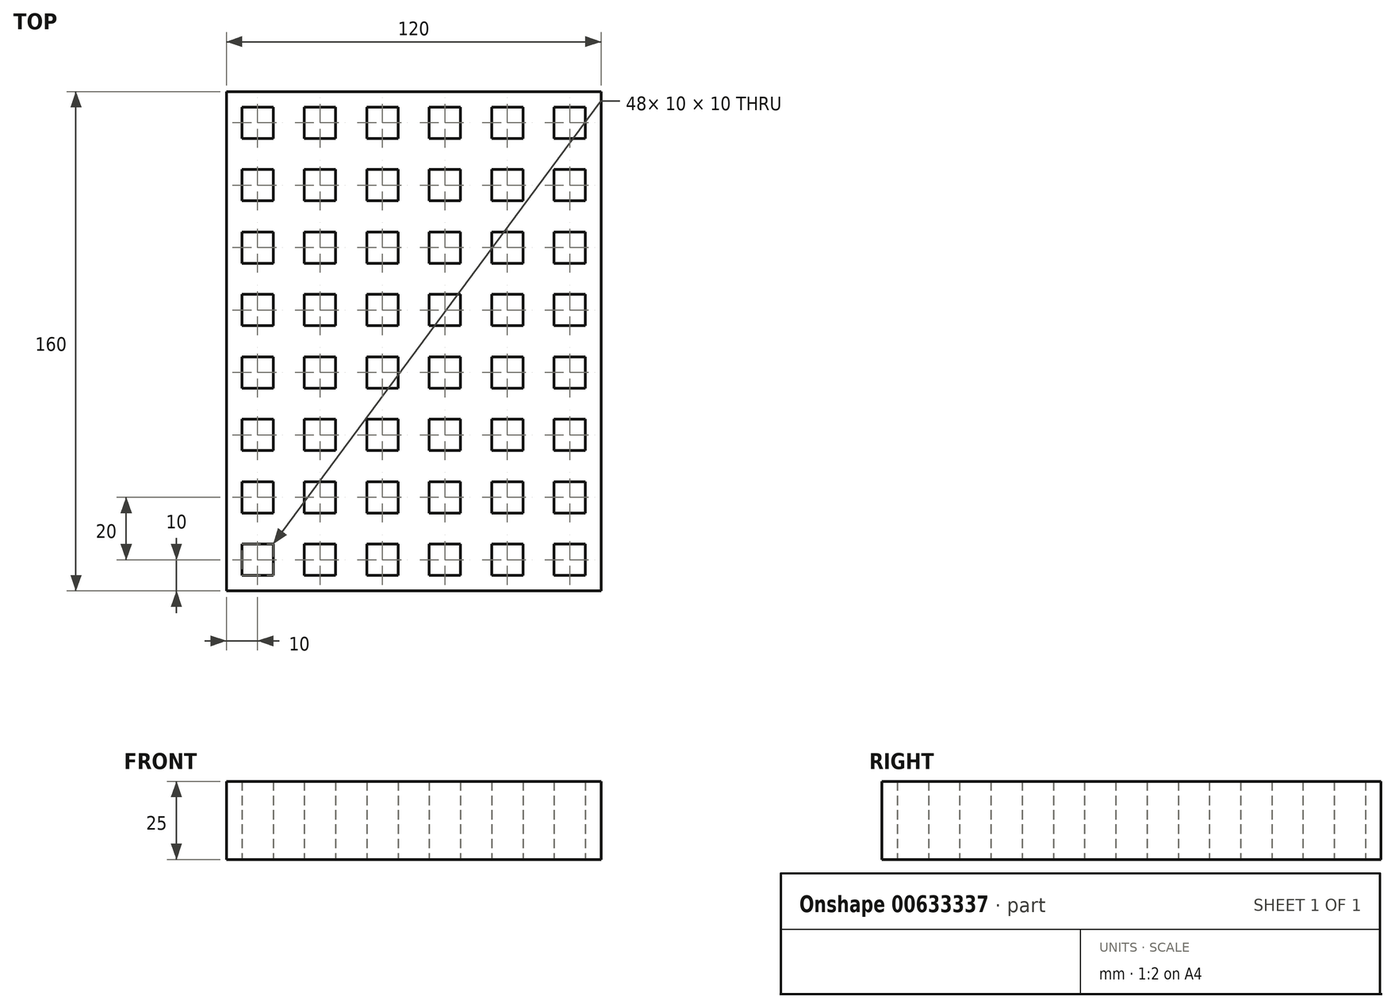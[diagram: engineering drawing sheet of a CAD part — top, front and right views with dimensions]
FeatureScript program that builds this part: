
annotation { "Feature Type Name" : "Feature", "Feature Type Description" : "" }
export const myFeature = defineFeature(function(context is Context, id is Id, definition is map)
    precondition{}
    {
        {
            var Q0;
            Q0=qCreatedBy(makeId("Top.planeOp"),FACE);
            var sketch = newSketch(context, id + "F0", { "sketchPlane" : qUnion([Q0])});
            skLineSegment(sketch, "E0.bottom", {"start": v(60, 80) * mm, "end": v(-60, 80) * mm});
            skLineSegment(sketch, "E0.top", {"start": v(60, -80) * mm, "end": v(-60, -80) * mm});
            skLineSegment(sketch, "E0.left", {"start": v(60, 80) * mm, "end": v(60, -80) * mm});
            skLineSegment(sketch, "E0.right", {"start": v(-60, 80) * mm, "end": v(-60, -80) * mm});
            skPoint(sketch, "E0.middle", {"position": v(0, 0) * mm});
            skLineSegment(sketch, "E1", {"start": v(-60, 80) * mm, "end": v(-60, 75) * mm, "construction": true});
            skLineSegment(sketch, "E2", {"start": v(-60, 75) * mm, "end": v(-55, 75) * mm, "construction": true});
            skLineSegment(sketch, "E3.bottom", {"start": v(-55, 75) * mm, "end": v(-45, 75) * mm});
            skLineSegment(sketch, "E3.top", {"start": v(-55, 65) * mm, "end": v(-45, 65) * mm});
            skLineSegment(sketch, "E3.left", {"start": v(-55, 75) * mm, "end": v(-55, 65) * mm});
            skLineSegment(sketch, "E3.right", {"start": v(-45, 75) * mm, "end": v(-45, 65) * mm});
            skLineSegment(sketch, "E4.0.1.0", {"start": v(-55, 55) * mm, "end": v(-45, 55) * mm});
            skLineSegment(sketch, "E4.0.1.1", {"start": v(-45, 55) * mm, "end": v(-45, 45) * mm});
            skLineSegment(sketch, "E4.0.1.2", {"start": v(-55, 45) * mm, "end": v(-45, 45) * mm});
            skLineSegment(sketch, "E4.0.1.3", {"start": v(-55, 55) * mm, "end": v(-55, 45) * mm});
            skLineSegment(sketch, "E4.0.2.0", {"start": v(-55, 35) * mm, "end": v(-45, 35) * mm});
            skLineSegment(sketch, "E4.0.2.1", {"start": v(-45, 35) * mm, "end": v(-45, 25) * mm});
            skLineSegment(sketch, "E4.0.2.2", {"start": v(-55, 25) * mm, "end": v(-45, 25) * mm});
            skLineSegment(sketch, "E4.0.2.3", {"start": v(-55, 35) * mm, "end": v(-55, 25) * mm});
            skLineSegment(sketch, "E4.0.3.0", {"start": v(-55, 15) * mm, "end": v(-45, 15) * mm});
            skLineSegment(sketch, "E4.0.3.1", {"start": v(-45, 15) * mm, "end": v(-45, 5) * mm});
            skLineSegment(sketch, "E4.0.3.2", {"start": v(-55, 5) * mm, "end": v(-45, 5) * mm});
            skLineSegment(sketch, "E4.0.3.3", {"start": v(-55, 15) * mm, "end": v(-55, 5) * mm});
            skLineSegment(sketch, "E4.0.4.0", {"start": v(-55, -5) * mm, "end": v(-45, -5) * mm});
            skLineSegment(sketch, "E4.0.4.1", {"start": v(-45, -5) * mm, "end": v(-45, -15) * mm});
            skLineSegment(sketch, "E4.0.4.2", {"start": v(-55, -15) * mm, "end": v(-45, -15) * mm});
            skLineSegment(sketch, "E4.0.4.3", {"start": v(-55, -5) * mm, "end": v(-55, -15) * mm});
            skLineSegment(sketch, "E4.0.5.0", {"start": v(-55, -25) * mm, "end": v(-45, -25) * mm});
            skLineSegment(sketch, "E4.0.5.1", {"start": v(-45, -25) * mm, "end": v(-45, -35) * mm});
            skLineSegment(sketch, "E4.0.5.2", {"start": v(-55, -35) * mm, "end": v(-45, -35) * mm});
            skLineSegment(sketch, "E4.0.5.3", {"start": v(-55, -25) * mm, "end": v(-55, -35) * mm});
            skLineSegment(sketch, "E4.0.6.0", {"start": v(-55, -45) * mm, "end": v(-45, -45) * mm});
            skLineSegment(sketch, "E4.0.6.1", {"start": v(-45, -45) * mm, "end": v(-45, -55) * mm});
            skLineSegment(sketch, "E4.0.6.2", {"start": v(-55, -55) * mm, "end": v(-45, -55) * mm});
            skLineSegment(sketch, "E4.0.6.3", {"start": v(-55, -45) * mm, "end": v(-55, -55) * mm});
            skLineSegment(sketch, "E4.0.7.0", {"start": v(-55, -65) * mm, "end": v(-45, -65) * mm});
            skLineSegment(sketch, "E4.0.7.1", {"start": v(-45, -65) * mm, "end": v(-45, -75) * mm});
            skLineSegment(sketch, "E4.0.7.2", {"start": v(-55, -75) * mm, "end": v(-45, -75) * mm});
            skLineSegment(sketch, "E4.0.7.3", {"start": v(-55, -65) * mm, "end": v(-55, -75) * mm});
            skLineSegment(sketch, "E4.1.0.0", {"start": v(-35, 75) * mm, "end": v(-25, 75) * mm});
            skLineSegment(sketch, "E4.1.0.1", {"start": v(-25, 75) * mm, "end": v(-25, 65) * mm});
            skLineSegment(sketch, "E4.1.0.2", {"start": v(-35, 65) * mm, "end": v(-25, 65) * mm});
            skLineSegment(sketch, "E4.1.0.3", {"start": v(-35, 75) * mm, "end": v(-35, 65) * mm});
            skLineSegment(sketch, "E4.1.1.0", {"start": v(-35, 55) * mm, "end": v(-25, 55) * mm});
            skLineSegment(sketch, "E4.1.1.1", {"start": v(-25, 55) * mm, "end": v(-25, 45) * mm});
            skLineSegment(sketch, "E4.1.1.2", {"start": v(-35, 45) * mm, "end": v(-25, 45) * mm});
            skLineSegment(sketch, "E4.1.1.3", {"start": v(-35, 55) * mm, "end": v(-35, 45) * mm});
            skLineSegment(sketch, "E4.1.2.0", {"start": v(-35, 35) * mm, "end": v(-25, 35) * mm});
            skLineSegment(sketch, "E4.1.2.1", {"start": v(-25, 35) * mm, "end": v(-25, 25) * mm});
            skLineSegment(sketch, "E4.1.2.2", {"start": v(-35, 25) * mm, "end": v(-25, 25) * mm});
            skLineSegment(sketch, "E4.1.2.3", {"start": v(-35, 35) * mm, "end": v(-35, 25) * mm});
            skLineSegment(sketch, "E4.1.3.0", {"start": v(-35, 15) * mm, "end": v(-25, 15) * mm});
            skLineSegment(sketch, "E4.1.3.1", {"start": v(-25, 15) * mm, "end": v(-25, 5) * mm});
            skLineSegment(sketch, "E4.1.3.2", {"start": v(-35, 5) * mm, "end": v(-25, 5) * mm});
            skLineSegment(sketch, "E4.1.3.3", {"start": v(-35, 15) * mm, "end": v(-35, 5) * mm});
            skLineSegment(sketch, "E4.1.4.0", {"start": v(-35, -5) * mm, "end": v(-25, -5) * mm});
            skLineSegment(sketch, "E4.1.4.1", {"start": v(-25, -5) * mm, "end": v(-25, -15) * mm});
            skLineSegment(sketch, "E4.1.4.2", {"start": v(-35, -15) * mm, "end": v(-25, -15) * mm});
            skLineSegment(sketch, "E4.1.4.3", {"start": v(-35, -5) * mm, "end": v(-35, -15) * mm});
            skLineSegment(sketch, "E4.1.5.0", {"start": v(-35, -25) * mm, "end": v(-25, -25) * mm});
            skLineSegment(sketch, "E4.1.5.1", {"start": v(-25, -25) * mm, "end": v(-25, -35) * mm});
            skLineSegment(sketch, "E4.1.5.2", {"start": v(-35, -35) * mm, "end": v(-25, -35) * mm});
            skLineSegment(sketch, "E4.1.5.3", {"start": v(-35, -25) * mm, "end": v(-35, -35) * mm});
            skLineSegment(sketch, "E4.1.6.0", {"start": v(-35, -45) * mm, "end": v(-25, -45) * mm});
            skLineSegment(sketch, "E4.1.6.1", {"start": v(-25, -45) * mm, "end": v(-25, -55) * mm});
            skLineSegment(sketch, "E4.1.6.2", {"start": v(-35, -55) * mm, "end": v(-25, -55) * mm});
            skLineSegment(sketch, "E4.1.6.3", {"start": v(-35, -45) * mm, "end": v(-35, -55) * mm});
            skLineSegment(sketch, "E4.1.7.0", {"start": v(-35, -65) * mm, "end": v(-25, -65) * mm});
            skLineSegment(sketch, "E4.1.7.1", {"start": v(-25, -65) * mm, "end": v(-25, -75) * mm});
            skLineSegment(sketch, "E4.1.7.2", {"start": v(-35, -75) * mm, "end": v(-25, -75) * mm});
            skLineSegment(sketch, "E4.1.7.3", {"start": v(-35, -65) * mm, "end": v(-35, -75) * mm});
            skLineSegment(sketch, "E4.2.0.0", {"start": v(-15, 75) * mm, "end": v(-5, 75) * mm});
            skLineSegment(sketch, "E4.2.0.1", {"start": v(-5, 75) * mm, "end": v(-5, 65) * mm});
            skLineSegment(sketch, "E4.2.0.2", {"start": v(-15, 65) * mm, "end": v(-5, 65) * mm});
            skLineSegment(sketch, "E4.2.0.3", {"start": v(-15, 75) * mm, "end": v(-15, 65) * mm});
            skLineSegment(sketch, "E4.2.1.0", {"start": v(-15, 55) * mm, "end": v(-5, 55) * mm});
            skLineSegment(sketch, "E4.2.1.1", {"start": v(-5, 55) * mm, "end": v(-5, 45) * mm});
            skLineSegment(sketch, "E4.2.1.2", {"start": v(-15, 45) * mm, "end": v(-5, 45) * mm});
            skLineSegment(sketch, "E4.2.1.3", {"start": v(-15, 55) * mm, "end": v(-15, 45) * mm});
            skLineSegment(sketch, "E4.2.2.0", {"start": v(-15, 35) * mm, "end": v(-5, 35) * mm});
            skLineSegment(sketch, "E4.2.2.1", {"start": v(-5, 35) * mm, "end": v(-5, 25) * mm});
            skLineSegment(sketch, "E4.2.2.2", {"start": v(-15, 25) * mm, "end": v(-5, 25) * mm});
            skLineSegment(sketch, "E4.2.2.3", {"start": v(-15, 35) * mm, "end": v(-15, 25) * mm});
            skLineSegment(sketch, "E4.2.3.0", {"start": v(-15, 15) * mm, "end": v(-5, 15) * mm});
            skLineSegment(sketch, "E4.2.3.1", {"start": v(-5, 15) * mm, "end": v(-5, 5) * mm});
            skLineSegment(sketch, "E4.2.3.2", {"start": v(-15, 5) * mm, "end": v(-5, 5) * mm});
            skLineSegment(sketch, "E4.2.3.3", {"start": v(-15, 15) * mm, "end": v(-15, 5) * mm});
            skLineSegment(sketch, "E4.2.4.0", {"start": v(-15, -5) * mm, "end": v(-5, -5) * mm});
            skLineSegment(sketch, "E4.2.4.1", {"start": v(-5, -5) * mm, "end": v(-5, -15) * mm});
            skLineSegment(sketch, "E4.2.4.2", {"start": v(-15, -15) * mm, "end": v(-5, -15) * mm});
            skLineSegment(sketch, "E4.2.4.3", {"start": v(-15, -5) * mm, "end": v(-15, -15) * mm});
            skLineSegment(sketch, "E4.2.5.0", {"start": v(-15, -25) * mm, "end": v(-5, -25) * mm});
            skLineSegment(sketch, "E4.2.5.1", {"start": v(-5, -25) * mm, "end": v(-5, -35) * mm});
            skLineSegment(sketch, "E4.2.5.2", {"start": v(-15, -35) * mm, "end": v(-5, -35) * mm});
            skLineSegment(sketch, "E4.2.5.3", {"start": v(-15, -25) * mm, "end": v(-15, -35) * mm});
            skLineSegment(sketch, "E4.2.6.0", {"start": v(-15, -45) * mm, "end": v(-5, -45) * mm});
            skLineSegment(sketch, "E4.2.6.1", {"start": v(-5, -45) * mm, "end": v(-5, -55) * mm});
            skLineSegment(sketch, "E4.2.6.2", {"start": v(-15, -55) * mm, "end": v(-5, -55) * mm});
            skLineSegment(sketch, "E4.2.6.3", {"start": v(-15, -45) * mm, "end": v(-15, -55) * mm});
            skLineSegment(sketch, "E4.2.7.0", {"start": v(-15, -65) * mm, "end": v(-5, -65) * mm});
            skLineSegment(sketch, "E4.2.7.1", {"start": v(-5, -65) * mm, "end": v(-5, -75) * mm});
            skLineSegment(sketch, "E4.2.7.2", {"start": v(-15, -75) * mm, "end": v(-5, -75) * mm});
            skLineSegment(sketch, "E4.2.7.3", {"start": v(-15, -65) * mm, "end": v(-15, -75) * mm});
            skLineSegment(sketch, "E4.3.0.0", {"start": v(5, 75) * mm, "end": v(15, 75) * mm});
            skLineSegment(sketch, "E4.3.0.1", {"start": v(15, 75) * mm, "end": v(15, 65) * mm});
            skLineSegment(sketch, "E4.3.0.2", {"start": v(5, 65) * mm, "end": v(15, 65) * mm});
            skLineSegment(sketch, "E4.3.0.3", {"start": v(5, 75) * mm, "end": v(5, 65) * mm});
            skLineSegment(sketch, "E4.3.1.0", {"start": v(5, 55) * mm, "end": v(15, 55) * mm});
            skLineSegment(sketch, "E4.3.1.1", {"start": v(15, 55) * mm, "end": v(15, 45) * mm});
            skLineSegment(sketch, "E4.3.1.2", {"start": v(5, 45) * mm, "end": v(15, 45) * mm});
            skLineSegment(sketch, "E4.3.1.3", {"start": v(5, 55) * mm, "end": v(5, 45) * mm});
            skLineSegment(sketch, "E4.3.2.0", {"start": v(5, 35) * mm, "end": v(15, 35) * mm});
            skLineSegment(sketch, "E4.3.2.1", {"start": v(15, 35) * mm, "end": v(15, 25) * mm});
            skLineSegment(sketch, "E4.3.2.2", {"start": v(5, 25) * mm, "end": v(15, 25) * mm});
            skLineSegment(sketch, "E4.3.2.3", {"start": v(5, 35) * mm, "end": v(5, 25) * mm});
            skLineSegment(sketch, "E4.3.3.0", {"start": v(5, 15) * mm, "end": v(15, 15) * mm});
            skLineSegment(sketch, "E4.3.3.1", {"start": v(15, 15) * mm, "end": v(15, 5) * mm});
            skLineSegment(sketch, "E4.3.3.2", {"start": v(5, 5) * mm, "end": v(15, 5) * mm});
            skLineSegment(sketch, "E4.3.3.3", {"start": v(5, 15) * mm, "end": v(5, 5) * mm});
            skLineSegment(sketch, "E4.3.4.0", {"start": v(5, -5) * mm, "end": v(15, -5) * mm});
            skLineSegment(sketch, "E4.3.4.1", {"start": v(15, -5) * mm, "end": v(15, -15) * mm});
            skLineSegment(sketch, "E4.3.4.2", {"start": v(5, -15) * mm, "end": v(15, -15) * mm});
            skLineSegment(sketch, "E4.3.4.3", {"start": v(5, -5) * mm, "end": v(5, -15) * mm});
            skLineSegment(sketch, "E4.3.5.0", {"start": v(5, -25) * mm, "end": v(15, -25) * mm});
            skLineSegment(sketch, "E4.3.5.1", {"start": v(15, -25) * mm, "end": v(15, -35) * mm});
            skLineSegment(sketch, "E4.3.5.2", {"start": v(5, -35) * mm, "end": v(15, -35) * mm});
            skLineSegment(sketch, "E4.3.5.3", {"start": v(5, -25) * mm, "end": v(5, -35) * mm});
            skLineSegment(sketch, "E4.3.6.0", {"start": v(5, -45) * mm, "end": v(15, -45) * mm});
            skLineSegment(sketch, "E4.3.6.1", {"start": v(15, -45) * mm, "end": v(15, -55) * mm});
            skLineSegment(sketch, "E4.3.6.2", {"start": v(5, -55) * mm, "end": v(15, -55) * mm});
            skLineSegment(sketch, "E4.3.6.3", {"start": v(5, -45) * mm, "end": v(5, -55) * mm});
            skLineSegment(sketch, "E4.3.7.0", {"start": v(5, -65) * mm, "end": v(15, -65) * mm});
            skLineSegment(sketch, "E4.3.7.1", {"start": v(15, -65) * mm, "end": v(15, -75) * mm});
            skLineSegment(sketch, "E4.3.7.2", {"start": v(5, -75) * mm, "end": v(15, -75) * mm});
            skLineSegment(sketch, "E4.3.7.3", {"start": v(5, -65) * mm, "end": v(5, -75) * mm});
            skLineSegment(sketch, "E4.4.0.0", {"start": v(25, 75) * mm, "end": v(35, 75) * mm});
            skLineSegment(sketch, "E4.4.0.1", {"start": v(35, 75) * mm, "end": v(35, 65) * mm});
            skLineSegment(sketch, "E4.4.0.2", {"start": v(25, 65) * mm, "end": v(35, 65) * mm});
            skLineSegment(sketch, "E4.4.0.3", {"start": v(25, 75) * mm, "end": v(25, 65) * mm});
            skLineSegment(sketch, "E4.4.1.0", {"start": v(25, 55) * mm, "end": v(35, 55) * mm});
            skLineSegment(sketch, "E4.4.1.1", {"start": v(35, 55) * mm, "end": v(35, 45) * mm});
            skLineSegment(sketch, "E4.4.1.2", {"start": v(25, 45) * mm, "end": v(35, 45) * mm});
            skLineSegment(sketch, "E4.4.1.3", {"start": v(25, 55) * mm, "end": v(25, 45) * mm});
            skLineSegment(sketch, "E4.4.2.0", {"start": v(25, 35) * mm, "end": v(35, 35) * mm});
            skLineSegment(sketch, "E4.4.2.1", {"start": v(35, 35) * mm, "end": v(35, 25) * mm});
            skLineSegment(sketch, "E4.4.2.2", {"start": v(25, 25) * mm, "end": v(35, 25) * mm});
            skLineSegment(sketch, "E4.4.2.3", {"start": v(25, 35) * mm, "end": v(25, 25) * mm});
            skLineSegment(sketch, "E4.4.3.0", {"start": v(25, 15) * mm, "end": v(35, 15) * mm});
            skLineSegment(sketch, "E4.4.3.1", {"start": v(35, 15) * mm, "end": v(35, 5) * mm});
            skLineSegment(sketch, "E4.4.3.2", {"start": v(25, 5) * mm, "end": v(35, 5) * mm});
            skLineSegment(sketch, "E4.4.3.3", {"start": v(25, 15) * mm, "end": v(25, 5) * mm});
            skLineSegment(sketch, "E4.4.4.0", {"start": v(25, -5) * mm, "end": v(35, -5) * mm});
            skLineSegment(sketch, "E4.4.4.1", {"start": v(35, -5) * mm, "end": v(35, -15) * mm});
            skLineSegment(sketch, "E4.4.4.2", {"start": v(25, -15) * mm, "end": v(35, -15) * mm});
            skLineSegment(sketch, "E4.4.4.3", {"start": v(25, -5) * mm, "end": v(25, -15) * mm});
            skLineSegment(sketch, "E4.4.5.0", {"start": v(25, -25) * mm, "end": v(35, -25) * mm});
            skLineSegment(sketch, "E4.4.5.1", {"start": v(35, -25) * mm, "end": v(35, -35) * mm});
            skLineSegment(sketch, "E4.4.5.2", {"start": v(25, -35) * mm, "end": v(35, -35) * mm});
            skLineSegment(sketch, "E4.4.5.3", {"start": v(25, -25) * mm, "end": v(25, -35) * mm});
            skLineSegment(sketch, "E4.4.6.0", {"start": v(25, -45) * mm, "end": v(35, -45) * mm});
            skLineSegment(sketch, "E4.4.6.1", {"start": v(35, -45) * mm, "end": v(35, -55) * mm});
            skLineSegment(sketch, "E4.4.6.2", {"start": v(25, -55) * mm, "end": v(35, -55) * mm});
            skLineSegment(sketch, "E4.4.6.3", {"start": v(25, -45) * mm, "end": v(25, -55) * mm});
            skLineSegment(sketch, "E4.4.7.0", {"start": v(25, -65) * mm, "end": v(35, -65) * mm});
            skLineSegment(sketch, "E4.4.7.1", {"start": v(35, -65) * mm, "end": v(35, -75) * mm});
            skLineSegment(sketch, "E4.4.7.2", {"start": v(25, -75) * mm, "end": v(35, -75) * mm});
            skLineSegment(sketch, "E4.4.7.3", {"start": v(25, -65) * mm, "end": v(25, -75) * mm});
            skLineSegment(sketch, "E4.5.0.0", {"start": v(45, 75) * mm, "end": v(55, 75) * mm});
            skLineSegment(sketch, "E4.5.0.1", {"start": v(55, 75) * mm, "end": v(55, 65) * mm});
            skLineSegment(sketch, "E4.5.0.2", {"start": v(45, 65) * mm, "end": v(55, 65) * mm});
            skLineSegment(sketch, "E4.5.0.3", {"start": v(45, 75) * mm, "end": v(45, 65) * mm});
            skLineSegment(sketch, "E4.5.1.0", {"start": v(45, 55) * mm, "end": v(55, 55) * mm});
            skLineSegment(sketch, "E4.5.1.1", {"start": v(55, 55) * mm, "end": v(55, 45) * mm});
            skLineSegment(sketch, "E4.5.1.2", {"start": v(45, 45) * mm, "end": v(55, 45) * mm});
            skLineSegment(sketch, "E4.5.1.3", {"start": v(45, 55) * mm, "end": v(45, 45) * mm});
            skLineSegment(sketch, "E4.5.2.0", {"start": v(45, 35) * mm, "end": v(55, 35) * mm});
            skLineSegment(sketch, "E4.5.2.1", {"start": v(55, 35) * mm, "end": v(55, 25) * mm});
            skLineSegment(sketch, "E4.5.2.2", {"start": v(45, 25) * mm, "end": v(55, 25) * mm});
            skLineSegment(sketch, "E4.5.2.3", {"start": v(45, 35) * mm, "end": v(45, 25) * mm});
            skLineSegment(sketch, "E4.5.3.0", {"start": v(45, 15) * mm, "end": v(55, 15) * mm});
            skLineSegment(sketch, "E4.5.3.1", {"start": v(55, 15) * mm, "end": v(55, 5) * mm});
            skLineSegment(sketch, "E4.5.3.2", {"start": v(45, 5) * mm, "end": v(55, 5) * mm});
            skLineSegment(sketch, "E4.5.3.3", {"start": v(45, 15) * mm, "end": v(45, 5) * mm});
            skLineSegment(sketch, "E4.5.4.0", {"start": v(45, -5) * mm, "end": v(55, -5) * mm});
            skLineSegment(sketch, "E4.5.4.1", {"start": v(55, -5) * mm, "end": v(55, -15) * mm});
            skLineSegment(sketch, "E4.5.4.2", {"start": v(45, -15) * mm, "end": v(55, -15) * mm});
            skLineSegment(sketch, "E4.5.4.3", {"start": v(45, -5) * mm, "end": v(45, -15) * mm});
            skLineSegment(sketch, "E4.5.5.0", {"start": v(45, -25) * mm, "end": v(55, -25) * mm});
            skLineSegment(sketch, "E4.5.5.1", {"start": v(55, -25) * mm, "end": v(55, -35) * mm});
            skLineSegment(sketch, "E4.5.5.2", {"start": v(45, -35) * mm, "end": v(55, -35) * mm});
            skLineSegment(sketch, "E4.5.5.3", {"start": v(45, -25) * mm, "end": v(45, -35) * mm});
            skLineSegment(sketch, "E4.5.6.0", {"start": v(45, -45) * mm, "end": v(55, -45) * mm});
            skLineSegment(sketch, "E4.5.6.1", {"start": v(55, -45) * mm, "end": v(55, -55) * mm});
            skLineSegment(sketch, "E4.5.6.2", {"start": v(45, -55) * mm, "end": v(55, -55) * mm});
            skLineSegment(sketch, "E4.5.6.3", {"start": v(45, -45) * mm, "end": v(45, -55) * mm});
            skLineSegment(sketch, "E4.5.7.0", {"start": v(45, -65) * mm, "end": v(55, -65) * mm});
            skLineSegment(sketch, "E4.5.7.1", {"start": v(55, -65) * mm, "end": v(55, -75) * mm});
            skLineSegment(sketch, "E4.5.7.2", {"start": v(45, -75) * mm, "end": v(55, -75) * mm});
            skLineSegment(sketch, "E4.5.7.3", {"start": v(45, -65) * mm, "end": v(45, -75) * mm});
            skLineSegment(sketch, "E4.direction1", {"start": v(-55, 75) * mm, "end": v(-35, 75) * mm, "construction": true});
            skLineSegment(sketch, "E4.direction2", {"start": v(-55, 75) * mm, "end": v(-55, 55) * mm, "construction": true});
            skSolve(sketch);
        }
        {
            var Q0;
            Q0=makeQuery(id+"F0.imprint","IMPRINT",FACE,{"disambiguationData":[TD([[makeQuery(id+"F0.imprint","IMPRINT",EDGE,{"derivedFrom":sQuery(id+"F0.wireOp",EDGE,"E0.bottom")}),1.0]])]});
            extrude(context, id + "F1", {"entities" : qUnion([Q0]), "depth" : 25 * mm, "offsetDistance" : 25 * mm});
        }
    });
